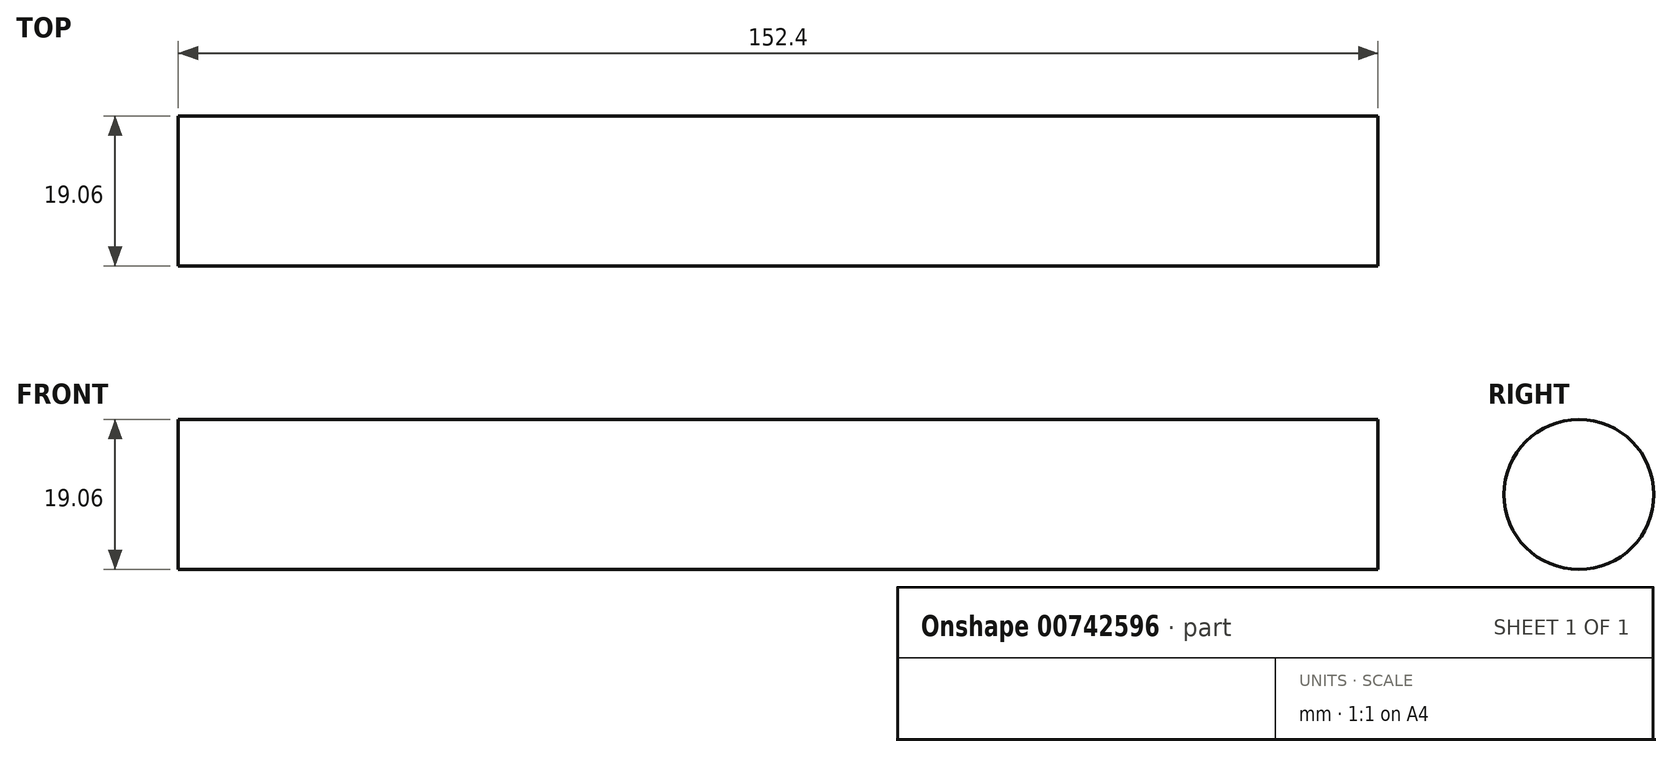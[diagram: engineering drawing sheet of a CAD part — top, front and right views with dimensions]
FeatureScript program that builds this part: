
annotation { "Feature Type Name" : "Feature", "Feature Type Description" : "" }
export const myFeature = defineFeature(function(context is Context, id is Id, definition is map)
    precondition{}
    {
        {
            var Q0;
            Q0=qCreatedBy(makeId("Right.planeOp"),FACE);
            var sketch = newSketch(context, id + "F0", { "sketchPlane" : qUnion([Q0])});
            skCircle(sketch, "E0", {"center": v(0, 0) * mm, "radius": 9.53 * mm});
            skSolve(sketch);
        }
        {
            var Q0;
            Q0 = qSketchRegion(id + "F0", true);
            extrude(context, id + "F1", {"entities" : qUnion([Q0]), "depth" : 152.4 * mm, "offsetDistance" : 25.4 * mm});
        }
    });
